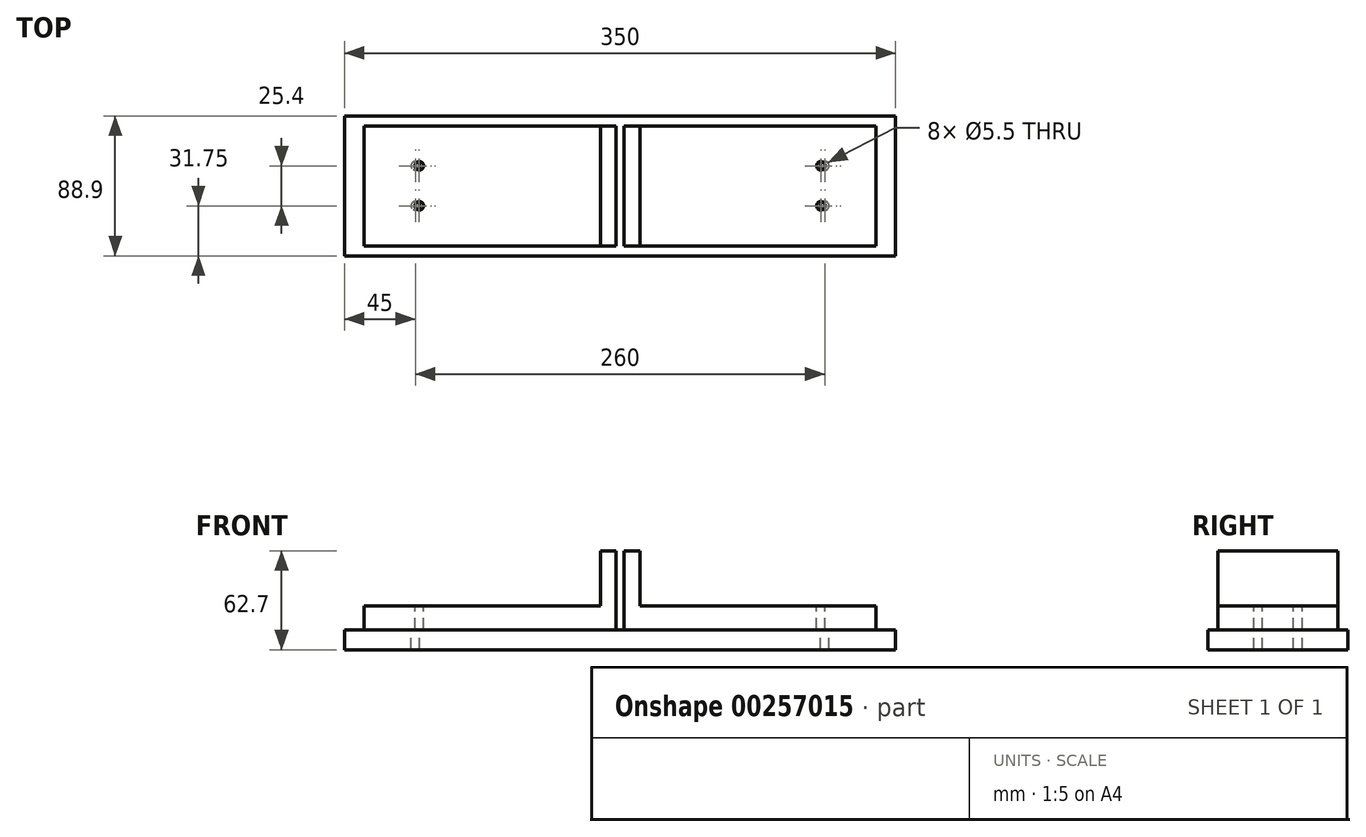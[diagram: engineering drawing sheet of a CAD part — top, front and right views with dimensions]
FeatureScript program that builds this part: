
annotation { "Feature Type Name" : "Feature", "Feature Type Description" : "" }
export const myFeature = defineFeature(function(context is Context, id is Id, definition is map)
    precondition{}
    {
        {
            var Q0;
            Q0=qCreatedBy(makeId("Front.planeOp"),FACE);
            var sketch = newSketch(context, id + "F0", { "sketchPlane" : qUnion([Q0])});
            skLineSegment(sketch, "E0", {"start": v(-162.54, 15) * mm, "end": v(-12.54, 15) * mm});
            skLineSegment(sketch, "E1", {"start": v(-12.54, 15) * mm, "end": v(-12.54, 50) * mm});
            skLineSegment(sketch, "E2", {"start": v(-12.54, 50) * mm, "end": v(-2.54, 50) * mm});
            skLineSegment(sketch, "E3", {"start": v(-2.54, 50) * mm, "end": v(-2.54, 0) * mm});
            skLineSegment(sketch, "E4", {"start": v(-2.54, 0) * mm, "end": v(-162.54, 0) * mm});
            skLineSegment(sketch, "E5", {"start": v(-162.54, 0) * mm, "end": v(-162.54, 15) * mm});
            skLineSegment(sketch, "E6", {"start": v(0, 0) * mm, "end": v(0, 149.94) * mm, "construction": true});
            skLineSegment(sketch, "E7.MirrorCS", {"start": v(12.54, 50) * mm, "end": v(2.54, 50) * mm});
            skLineSegment(sketch, "E8.MirrorCS", {"start": v(162.54, 0) * mm, "end": v(162.54, 15) * mm});
            skLineSegment(sketch, "E9.MirrorCS", {"start": v(162.54, 15) * mm, "end": v(12.54, 15) * mm});
            skLineSegment(sketch, "E10.MirrorCS", {"start": v(12.54, 15) * mm, "end": v(12.54, 50) * mm});
            skLineSegment(sketch, "E11.MirrorCS", {"start": v(2.54, 50) * mm, "end": v(2.54, 0) * mm});
            skLineSegment(sketch, "E12.MirrorCS", {"start": v(2.54, 0) * mm, "end": v(162.54, 0) * mm});
            skSolve(sketch);
        }
        {
            var Q0;
            Q0 = qSketchRegion(id + "F0", true);
            extrude(context, id + "F1", {"entities" : qUnion([Q0]), "endBound" : BoundingType.SYMMETRIC, "depth" : 76.2 * mm});
        }
        {
            var Q0;
            Q0=qCreatedBy(makeId("Top.planeOp"),FACE);
            var sketch = newSketch(context, id + "F2", { "sketchPlane" : qUnion([Q0])});
            skLineSegment(sketch, "E13.bottom", {"start": v(175, -44.45) * mm, "end": v(-175, -44.45) * mm});
            skLineSegment(sketch, "E13.top", {"start": v(175, 44.45) * mm, "end": v(-175, 44.45) * mm});
            skLineSegment(sketch, "E13.left", {"start": v(175, -44.45) * mm, "end": v(175, 44.45) * mm});
            skLineSegment(sketch, "E13.right", {"start": v(-175, -44.45) * mm, "end": v(-175, 44.45) * mm});
            skPoint(sketch, "E13.middle", {"position": v(0, 0) * mm});
            skCircle(sketch, "E14", {"center": v(-130, -12.7) * mm, "radius": 2.75 * mm});
            skLineSegment(sketch, "E15", {"start": v(0, 0) * mm, "end": v(44.56, 0) * mm, "construction": true});
            skLineSegment(sketch, "E16", {"start": v(0, 0) * mm, "end": v(0, 55.72) * mm, "construction": true});
            skPoint(sketch, "E16.endSnap0", {"position": v(0, 44.45) * mm});
            skCircle(sketch, "E17.MirrorC", {"center": v(-130, 12.7) * mm, "radius": 2.75 * mm});
            skCircle(sketch, "E18.MirrorC", {"center": v(130, -12.7) * mm, "radius": 2.75 * mm});
            skCircle(sketch, "E19.MirrorC", {"center": v(130, 12.7) * mm, "radius": 2.75 * mm});
            skSolve(sketch);
        }
        {
            var Q0;
            Q0 = qSketchRegion(id + "F2", true);
            extrude(context, id + "F3", {"entities" : qUnion([Q0]), "oppositeDirection" : true, "depth" : 12.7 * mm});
        }
        {
            var Q0;
            Q0=makeQuery(id+"F1.opExtrude","SWEPT_FACE",FACE,{"disambiguationData":[OSD([sQuery(id+"F0.wireOp",EDGE,"E0")])]});
            var sketch = newSketch(context, id + "F4", { "sketchPlane" : qUnion([Q0])});
            skCircle(sketch, "E20", {"center": v(-127.54, -12.7) * mm, "radius": 2.75 * mm});
            skLineSegment(sketch, "E21", {"start": v(0, 0) * mm, "end": v(26.25, 0) * mm, "construction": true});
            skLineSegment(sketch, "E22", {"start": v(0, 0) * mm, "end": v(0, 62.96) * mm, "construction": true});
            skLineSegment(sketch, "E23.MirrorCS", {"start": v(0, 0) * mm, "end": v(-26.25, 0) * mm, "construction": true});
            skCircle(sketch, "E24.MirrorC", {"center": v(127.54, -12.7) * mm, "radius": 2.75 * mm});
            skCircle(sketch, "E25.MirrorC", {"center": v(127.54, 12.7) * mm, "radius": 2.75 * mm});
            skCircle(sketch, "E26.MirrorC", {"center": v(-127.54, 12.7) * mm, "radius": 2.75 * mm});
            skSolve(sketch);
        }
        {
            var Q0;
            Q0 = qSketchRegion(id + "F4", true);
            var Q1;
            Q1=makeQuery(id+"F3.opExtrude","CAP_FACE",FACE,{"disambiguationData":[OSD([sQuery(id+"F2.wireOp",EDGE,"E13.bottom"),sQuery(id+"F2.wireOp",EDGE,"E13.top"),sQuery(id+"F2.wireOp",EDGE,"E13.left"),sQuery(id+"F2.wireOp",EDGE,"E13.right"),sQuery(id+"F2.wireOp",EDGE,"E14"),sQuery(id+"F2.wireOp",EDGE,"E17.MirrorC"),sQuery(id+"F2.wireOp",EDGE,"E18.MirrorC"),sQuery(id+"F2.wireOp",EDGE,"E19.MirrorC")])],"isStart":true});
            extrude(context, id + "F5", {"entities" : qUnion([Q0]), "operationType" : NewBodyOperationType.REMOVE, "endBound" : BoundingType.UP_TO_SURFACE, "oppositeDirection" : true, "endBoundEntityFace" : qUnion([Q1]), "depth" : 25.4 * mm});
        }
    });
